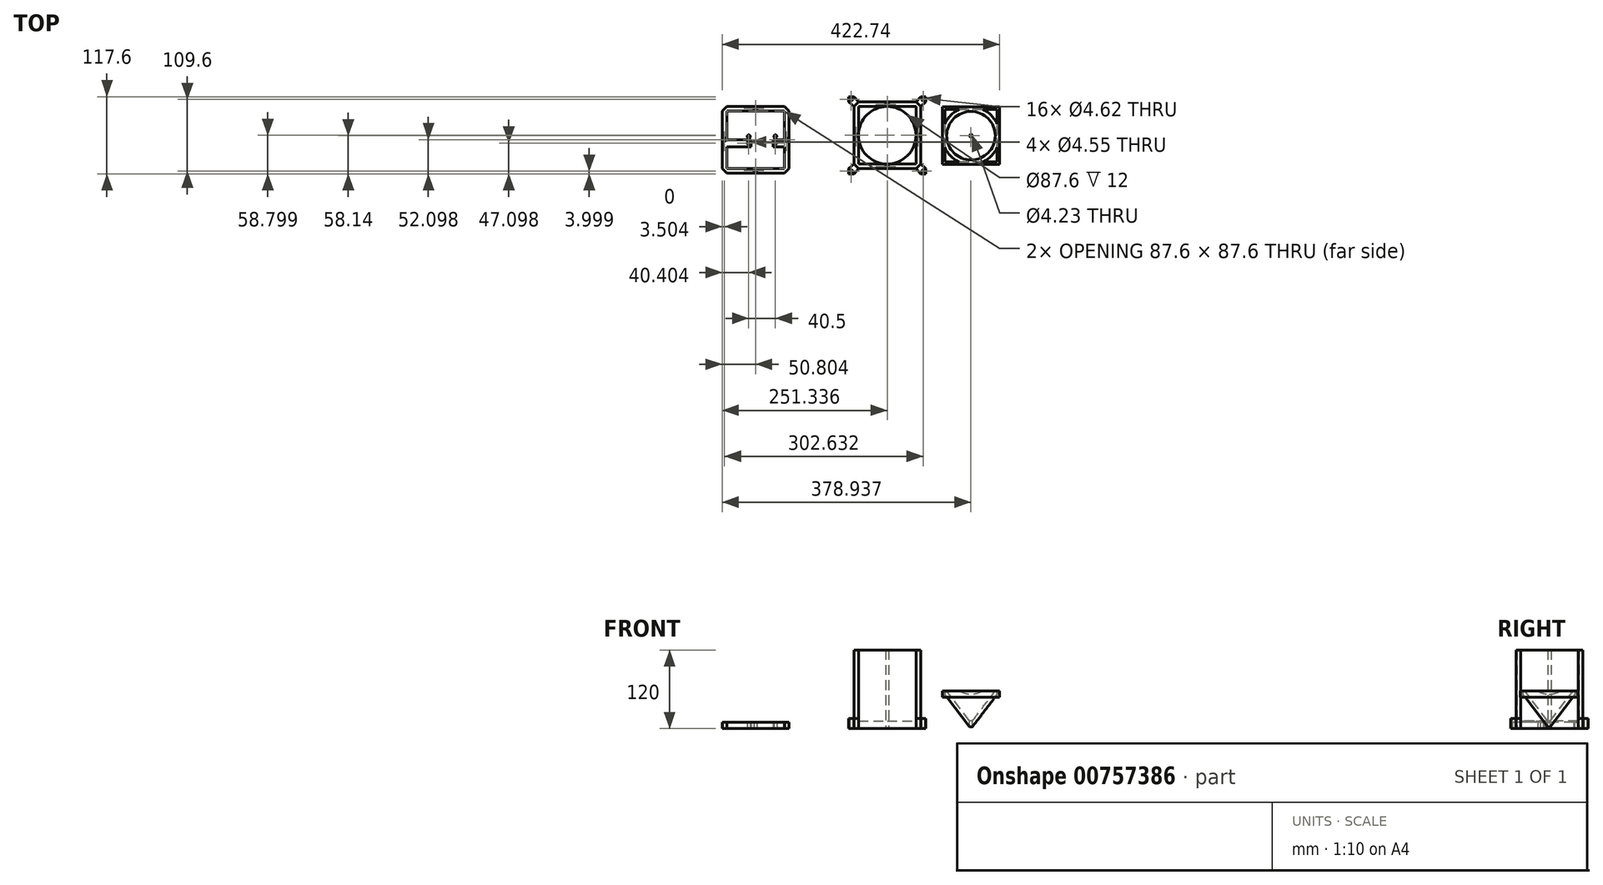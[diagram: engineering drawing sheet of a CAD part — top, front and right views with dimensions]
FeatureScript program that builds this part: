
annotation { "Feature Type Name" : "Feature", "Feature Type Description" : "" }
export const myFeature = defineFeature(function(context is Context, id is Id, definition is map)
    precondition{}
    {
        {
            var Q0;
            Q0=qCreatedBy(makeId("Top.planeOp"),FACE);
            var sketch = newSketch(context, id + "F0", { "sketchPlane" : qUnion([Q0])});
            skLineSegment(sketch, "E0.bottom", {"start": v(-49.4, 51.46) * mm, "end": v(38.2, 51.46) * mm});
            skLineSegment(sketch, "E0.top", {"start": v(-49.4, -50.14) * mm, "end": v(38.2, -50.14) * mm});
            skLineSegment(sketch, "E0.left", {"start": v(-56.4, 44.46) * mm, "end": v(-56.4, -43.14) * mm});
            skLineSegment(sketch, "E0.right", {"start": v(45.2, 44.46) * mm, "end": v(45.2, -43.14) * mm});
            skLineSegment(sketch, "E1.0", {"start": v(-49.4, 44.46) * mm, "end": v(38.2, 44.46) * mm});
            skLineSegment(sketch, "E1.1", {"start": v(-49.4, 44.46) * mm, "end": v(-49.4, -43.14) * mm});
            skLineSegment(sketch, "E1.2", {"start": v(-49.4, -43.14) * mm, "end": v(38.2, -43.14) * mm});
            skLineSegment(sketch, "E1.3", {"start": v(38.2, 44.46) * mm, "end": v(38.2, -43.14) * mm});
            skLineSegment(sketch, "E2.top", {"start": v(-56.4, 59.46) * mm, "end": v(-64.4, 59.46) * mm});
            skLineSegment(sketch, "E2.right", {"start": v(-64.4, 51.46) * mm, "end": v(-64.4, 59.46) * mm});
            skLineSegment(sketch, "E3.top", {"start": v(45.2, 59.46) * mm, "end": v(53.2, 59.46) * mm});
            skLineSegment(sketch, "E3.right", {"start": v(53.2, 51.46) * mm, "end": v(53.2, 59.46) * mm});
            skLineSegment(sketch, "E4.top", {"start": v(45.2, -58.14) * mm, "end": v(53.2, -58.14) * mm});
            skLineSegment(sketch, "E4.right", {"start": v(53.2, -50.14) * mm, "end": v(53.2, -58.14) * mm});
            skLineSegment(sketch, "E5.top", {"start": v(-56.4, -58.14) * mm, "end": v(-64.4, -58.14) * mm});
            skLineSegment(sketch, "E5.right", {"start": v(-64.4, -50.14) * mm, "end": v(-64.4, -58.14) * mm});
            skCircle(sketch, "E6", {"center": v(-60.4, 55.46) * mm, "radius": 2.31 * mm});
            skCircle(sketch, "E7", {"center": v(-60.4, -54.14) * mm, "radius": 2.31 * mm});
            skCircle(sketch, "E8", {"center": v(49.2, -54.14) * mm, "radius": 2.31 * mm});
            skCircle(sketch, "E9", {"center": v(49.2, 55.46) * mm, "radius": 2.31 * mm});
            skLineSegment(sketch, "E10", {"start": v(-64.4, 51.46) * mm, "end": v(-56.4, 44.46) * mm});
            skLineSegment(sketch, "E11", {"start": v(-56.4, 59.46) * mm, "end": v(-49.4, 51.46) * mm});
            skLineSegment(sketch, "E12", {"start": v(-64.4, -50.14) * mm, "end": v(-56.4, -43.14) * mm});
            skLineSegment(sketch, "E13", {"start": v(-56.4, -58.14) * mm, "end": v(-49.4, -50.14) * mm});
            skLineSegment(sketch, "E14", {"start": v(45.2, -58.14) * mm, "end": v(38.2, -50.14) * mm});
            skLineSegment(sketch, "E15", {"start": v(53.2, -50.14) * mm, "end": v(45.2, -43.14) * mm});
            skLineSegment(sketch, "E16", {"start": v(45.2, 59.46) * mm, "end": v(38.2, 51.46) * mm});
            skLineSegment(sketch, "E17", {"start": v(53.2, 51.46) * mm, "end": v(45.2, 44.46) * mm});
            skPoint(sketch, "E4.left.start.orphan", {"position": v(45.2, -50.14) * mm});
            skLineSegment(sketch, "E18", {"start": v(-56.4, 44.46) * mm, "end": v(-49.4, 51.46) * mm});
            skLineSegment(sketch, "E19", {"start": v(38.2, 51.46) * mm, "end": v(45.2, 44.46) * mm});
            skLineSegment(sketch, "E20", {"start": v(-56.4, -43.14) * mm, "end": v(-49.4, -50.14) * mm});
            skLineSegment(sketch, "E21", {"start": v(38.2, -50.14) * mm, "end": v(45.2, -43.14) * mm});
            skCircle(sketch, "E22", {"center": v(-5.6, 0.66) * mm, "radius": 43.8 * mm});
            skCircle(sketch, "E23", {"center": v(-5.6, 47.96) * mm, "radius": 2.31 * mm});
            skCircle(sketch, "E24", {"center": v(-52.9, 0.66) * mm, "radius": 2.31 * mm});
            skCircle(sketch, "E25", {"center": v(41.7, 0.66) * mm, "radius": 2.31 * mm});
            skCircle(sketch, "E26", {"center": v(-5.6, -46.64) * mm, "radius": 2.31 * mm});
            skLineSegment(sketch, "E27.bottom", {"start": v(-249.94, 44.76) * mm, "end": v(-162.34, 44.76) * mm});
            skLineSegment(sketch, "E27.top", {"start": v(-249.94, -56.84) * mm, "end": v(-162.34, -56.84) * mm});
            skLineSegment(sketch, "E27.left", {"start": v(-256.94, 37.76) * mm, "end": v(-256.94, -49.84) * mm});
            skLineSegment(sketch, "E27.right", {"start": v(-155.34, 37.76) * mm, "end": v(-155.34, -49.84) * mm});
            skLineSegment(sketch, "E28.0", {"start": v(-249.94, 37.76) * mm, "end": v(-162.34, 37.76) * mm});
            skLineSegment(sketch, "E28.1", {"start": v(-249.94, 37.76) * mm, "end": v(-249.94, -49.84) * mm});
            skLineSegment(sketch, "E28.2", {"start": v(-249.94, -49.84) * mm, "end": v(-162.34, -49.84) * mm});
            skLineSegment(sketch, "E28.3", {"start": v(-162.34, 37.76) * mm, "end": v(-162.34, -49.84) * mm});
            skLineSegment(sketch, "E29", {"start": v(-256.94, 37.76) * mm, "end": v(-249.94, 44.76) * mm});
            skLineSegment(sketch, "E30", {"start": v(-162.34, 44.76) * mm, "end": v(-155.34, 37.76) * mm});
            skLineSegment(sketch, "E31", {"start": v(-256.94, -49.84) * mm, "end": v(-249.94, -56.84) * mm});
            skLineSegment(sketch, "E32", {"start": v(-162.34, -56.84) * mm, "end": v(-155.34, -49.84) * mm});
            skCircle(sketch, "E33", {"center": v(-206.14, 41.26) * mm, "radius": 2.31 * mm});
            skCircle(sketch, "E34", {"center": v(-253.44, -6.04) * mm, "radius": 2.31 * mm});
            skCircle(sketch, "E35", {"center": v(-158.84, -6.04) * mm, "radius": 2.31 * mm});
            skCircle(sketch, "E36", {"center": v(-206.14, -53.34) * mm, "radius": 2.31 * mm});
            skPoint(sketch, "E37.middle", {"position": v(-206.14, -6.04) * mm});
            skPoint(sketch, "E37.middle.positionSnap0", {"position": v(-206.14, 37.76) * mm});
            skPoint(sketch, "E37.middle.positionSnap1", {"position": v(-249.94, -6.04) * mm});
            skPoint(sketch, "E37.centerSnap0", {"position": v(-206.14, 37.76) * mm});
            skPoint(sketch, "E37.centerSnap1", {"position": v(-249.94, -6.04) * mm});
            skCircle(sketch, "E38", {"center": v(-176.04, -11.04) * mm, "radius": 2.27 * mm});
            skCircle(sketch, "E39", {"center": v(-216.54, -11.04) * mm, "radius": 2.27 * mm});
            skLineSegment(sketch, "E40", {"start": v(-249.94, -6.04) * mm, "end": v(-162.34, -6.04) * mm});
            skCircle(sketch, "E41.MirrorC", {"center": v(-176.04, -1.04) * mm, "radius": 2.27 * mm});
            skCircle(sketch, "E42.MirrorC", {"center": v(-216.54, -1.04) * mm, "radius": 2.27 * mm});
            skLineSegment(sketch, "E43.bottom", {"start": v(-249.94, 6.48) * mm, "end": v(-213.04, 6.48) * mm});
            skLineSegment(sketch, "E43.top", {"start": v(-249.94, -16.78) * mm, "end": v(-213.04, -16.78) * mm});
            skLineSegment(sketch, "E43.left", {"start": v(-249.94, 6.48) * mm, "end": v(-249.94, -16.78) * mm});
            skLineSegment(sketch, "E43.right", {"start": v(-213.04, 6.48) * mm, "end": v(-213.04, -16.78) * mm});
            skLineSegment(sketch, "E44.bottom", {"start": v(-162.34, 6.48) * mm, "end": v(-179.54, 6.48) * mm});
            skLineSegment(sketch, "E44.top", {"start": v(-162.34, -16.78) * mm, "end": v(-179.54, -16.78) * mm});
            skLineSegment(sketch, "E44.left", {"start": v(-162.34, 6.48) * mm, "end": v(-162.34, -16.78) * mm});
            skLineSegment(sketch, "E44.right", {"start": v(-179.54, 6.48) * mm, "end": v(-179.54, -16.78) * mm});
            skSolve(sketch);
        }
        {
            var Q0;
            Q0=makeQuery(id+"F0.imprint","IMPRINT",FACE,{"disambiguationData":[TD([[makeQuery(id+"F0.imprint","IMPRINT",EDGE,{"derivedFrom":sQuery(id+"F0.wireOp",EDGE,"E0.bottom")}),-1.0]])]});
            extrude(context, id + "F1", {"entities" : qUnion([Q0]), "depth" : 120 * mm, "offsetDistance" : 25 * mm});
        }
        {
            var Q0;
            Q0=makeQuery(id+"F0.imprint","IMPRINT",FACE,{"disambiguationData":[TD([[makeQuery(id+"F0.imprint","IMPRINT",EDGE,{"derivedFrom":sQuery(id+"F0.wireOp",EDGE,"E5.top")}),-1.0]])]});
            var Q1;
            Q1=makeQuery(id+"F0.imprint","IMPRINT",FACE,{"disambiguationData":[TD([[makeQuery(id+"F0.imprint","IMPRINT",EDGE,{"derivedFrom":sQuery(id+"F0.wireOp",EDGE,"E4.top")}),1.0]])]});
            var Q2;
            Q2=makeQuery(id+"F0.imprint","IMPRINT",FACE,{"disambiguationData":[TD([[makeQuery(id+"F0.imprint","IMPRINT",EDGE,{"derivedFrom":sQuery(id+"F0.wireOp",EDGE,"E3.top")}),-1.0]])]});
            var Q3;
            Q3=makeQuery(id+"F0.imprint","IMPRINT",FACE,{"disambiguationData":[TD([[makeQuery(id+"F0.imprint","IMPRINT",EDGE,{"derivedFrom":sQuery(id+"F0.wireOp",EDGE,"E2.top")}),1.0]])]});
            extrude(context, id + "F2", {"entities" : qUnion([Q0, Q1, Q2, Q3]), "operationType" : NewBodyOperationType.ADD, "depth" : 15.5 * mm, "offsetDistance" : 25 * mm});
        }
        {
            var Q0;
            {var subQ0=sQuery(id+"F0.wireOp",EDGE,"E1.1");var subQ1=sQuery(id+"F0.wireOp",EDGE,"E1.0");var subQ2=makeQuery(id+"F0.imprint","INTERSECT",VERTEX,{"derivedFrom":[subQ1,subQ0]});Q0=makeQuery(id+"F0.imprint","IMPRINT",FACE,{"disambiguationData":[TD([[makeQuery(id+"F0.imprint","IMPRINT",EDGE,{"disambiguationData":[TD([[subQ2,-1.0]])],"derivedFrom":subQ1}),-1.0]])]});}
            var Q1;
            {var subQ0=sQuery(id+"F0.wireOp",EDGE,"E1.3");var subQ1=sQuery(id+"F0.wireOp",EDGE,"E1.0");var subQ2=makeQuery(id+"F0.imprint","INTERSECT",VERTEX,{"derivedFrom":[subQ1,subQ0]});Q1=makeQuery(id+"F0.imprint","IMPRINT",FACE,{"disambiguationData":[TD([[makeQuery(id+"F0.imprint","IMPRINT",EDGE,{"disambiguationData":[TD([[subQ2,1.0]])],"derivedFrom":subQ1}),-1.0]])]});}
            var Q2;
            {var subQ0=sQuery(id+"F0.wireOp",EDGE,"E1.3");var subQ1=sQuery(id+"F0.wireOp",EDGE,"E1.2");var subQ2=makeQuery(id+"F0.imprint","INTERSECT",VERTEX,{"derivedFrom":[subQ1,subQ0]});Q2=makeQuery(id+"F0.imprint","IMPRINT",FACE,{"disambiguationData":[TD([[makeQuery(id+"F0.imprint","IMPRINT",EDGE,{"disambiguationData":[TD([[subQ2,1.0]])],"derivedFrom":subQ1}),1.0]])]});}
            var Q3;
            {var subQ0=sQuery(id+"F0.wireOp",EDGE,"E1.2");var subQ1=sQuery(id+"F0.wireOp",EDGE,"E1.1");var subQ2=makeQuery(id+"F0.imprint","INTERSECT",VERTEX,{"derivedFrom":[subQ1,subQ0]});Q3=makeQuery(id+"F0.imprint","IMPRINT",FACE,{"disambiguationData":[TD([[makeQuery(id+"F0.imprint","IMPRINT",EDGE,{"disambiguationData":[TD([[subQ2,1.0]])],"derivedFrom":subQ1}),1.0]])]});}
            extrude(context, id + "F3", {"entities" : qUnion([Q0, Q1, Q2, Q3]), "operationType" : NewBodyOperationType.ADD, "depth" : 12 * mm, "offsetDistance" : 25 * mm});
        }
        {
            var Q0;
            Q0=qCreatedBy(makeId("Front.planeOp"),FACE);
            var sketch = newSketch(context, id + "F4", { "sketchPlane" : qUnion([Q0])});
            skLineSegment(sketch, "E45.bottom", {"start": v(78.2, 57.63) * mm, "end": v(85.04, 57.63) * mm});
            skLineSegment(sketch, "E45.right", {"start": v(122, 57.63) * mm, "end": v(122, 0) * mm});
            skLineSegment(sketch, "E46", {"start": v(78.2, 57.63) * mm, "end": v(119.88, 2.78) * mm});
            skLineSegment(sketch, "E47", {"start": v(85.04, 57.63) * mm, "end": v(119.88, 11.8) * mm});
            skLineSegment(sketch, "E48", {"start": v(119.88, 11.8) * mm, "end": v(119.88, 2.78) * mm});
            skSolve(sketch);
        }
        {
            var Q0;
            Q0=makeQuery(id+"F4.imprint","IMPRINT",FACE,{"disambiguationData":[TD([[makeQuery(id+"F4.imprint","IMPRINT",EDGE,{"derivedFrom":sQuery(id+"F4.wireOp",EDGE,"E45.bottom")}),-1.0]])]});
            var Q1;
            Q1=sQuery(id+"F4.wireOp",EDGE,"E45.right");
            revolve(context, id + "F5", {"surfaceOperationType" : NewSurfaceOperationType.NEW, "entities" : qUnion([Q0]), "axis" : qUnion([Q1]), "revolveType" : RevolveType.FULL});
        }
        {
            var Q0;
            Q0=makeQuery(id+"F5.opRevolve","SWEPT_FACE",FACE,{"disambiguationData":[OSD([sQuery(id+"F4.wireOp",EDGE,"E45.bottom")])]});
            var sketch = newSketch(context, id + "F6", { "sketchPlane" : qUnion([Q0])});
            skLineSegment(sketch, "E49.bottom", {"start": v(165.8, 43.8) * mm, "end": v(78.2, 43.8) * mm});
            skLineSegment(sketch, "E49.top", {"start": v(165.8, -43.8) * mm, "end": v(78.2, -43.8) * mm});
            skLineSegment(sketch, "E49.left", {"start": v(165.8, 43.8) * mm, "end": v(165.8, -43.8) * mm});
            skLineSegment(sketch, "E49.right", {"start": v(78.2, 43.8) * mm, "end": v(78.2, -43.8) * mm});
            skPoint(sketch, "E49.middle", {"position": v(122, 0) * mm});
            skLineSegment(sketch, "E50.bottom", {"start": v(162, 40) * mm, "end": v(82, 40) * mm});
            skLineSegment(sketch, "E50.top", {"start": v(162, -40) * mm, "end": v(82, -40) * mm});
            skLineSegment(sketch, "E50.left", {"start": v(162, 40) * mm, "end": v(162, -40) * mm});
            skLineSegment(sketch, "E50.right", {"start": v(82, 40) * mm, "end": v(82, -40) * mm});
            skSolve(sketch);
        }
        {
            var Q0;
            {var subQ6=sQuery(id+"F6.wireOp",EDGE,"E49.left");var subQ8=sQuery(id+"F6.wireOp",EDGE,"E49.bottom");var subQ9=makeQuery(id+"F6.imprint","INTERSECT",VERTEX,{"derivedFrom":[subQ8,subQ6]});Q0=makeQuery(id+"F6.imprint","IMPRINT",FACE,{"disambiguationData":[TD([[makeQuery(id+"F6.imprint","IMPRINT",EDGE,{"disambiguationData":[TD([[subQ9,-1.0]])],"derivedFrom":subQ8}),1.0]])]});}
            var Q1;
            {var subQ5=sQuery(id+"F6.wireOp",EDGE,"E49.right");var subQ6=sQuery(id+"F6.wireOp",EDGE,"E49.bottom");var subQ7=makeQuery(id+"F6.imprint","INTERSECT",VERTEX,{"derivedFrom":[subQ6,subQ5]});Q1=makeQuery(id+"F6.imprint","IMPRINT",FACE,{"disambiguationData":[TD([[makeQuery(id+"F6.imprint","IMPRINT",EDGE,{"disambiguationData":[TD([[subQ7,1.0]])],"derivedFrom":subQ6}),1.0]])]});}
            var Q2;
            {var subQ0=sQuery(id+"F6.wireOp",EDGE,"E50.right");var subQ1=makeQuery(id+"F5.opRevolve","SWEPT_EDGE",EDGE,{"disambiguationData":[OSD([sQuery(id+"F4.wireOp",EDGE,"E45.bottom"),sQuery(id+"F4.wireOp",EDGE,"E46")])]});var subQ2=makeQuery(id+"F6.imprint","INTERSECT",VERTEX,{"disambiguationData":[OD(0.0)],"derivedFrom":[subQ1,subQ0]});Q2=makeQuery(id+"F6.imprint","IMPRINT",FACE,{"disambiguationData":[TD([[makeQuery(id+"F6.imprint","IMPRINT",EDGE,{"disambiguationData":[TD([[subQ2,-1.0]])],"derivedFrom":subQ0}),-1.0]])]});}
            var Q3;
            {var subQ5=sQuery(id+"F6.wireOp",EDGE,"E49.right");var subQ6=sQuery(id+"F6.wireOp",EDGE,"E49.top");var subQ7=makeQuery(id+"F6.imprint","INTERSECT",VERTEX,{"derivedFrom":[subQ6,subQ5]});Q3=makeQuery(id+"F6.imprint","IMPRINT",FACE,{"disambiguationData":[TD([[makeQuery(id+"F6.imprint","IMPRINT",EDGE,{"disambiguationData":[TD([[subQ7,1.0]])],"derivedFrom":subQ6}),-1.0]])]});}
            var Q4;
            {var subQ5=sQuery(id+"F6.wireOp",EDGE,"E49.left");var subQ6=sQuery(id+"F6.wireOp",EDGE,"E49.top");var subQ7=makeQuery(id+"F6.imprint","INTERSECT",VERTEX,{"derivedFrom":[subQ6,subQ5]});Q4=makeQuery(id+"F6.imprint","IMPRINT",FACE,{"disambiguationData":[TD([[makeQuery(id+"F6.imprint","IMPRINT",EDGE,{"disambiguationData":[TD([[subQ7,-1.0]])],"derivedFrom":subQ6}),-1.0]])]});}
            var Q5;
            {var subQ0=sQuery(id+"F6.wireOp",EDGE,"E50.top");var subQ1=makeQuery(id+"F5.opRevolve","SWEPT_EDGE",EDGE,{"disambiguationData":[OSD([sQuery(id+"F4.wireOp",EDGE,"E45.bottom"),sQuery(id+"F4.wireOp",EDGE,"E46")])]});var subQ2=makeQuery(id+"F6.imprint","INTERSECT",VERTEX,{"disambiguationData":[OD(0.0)],"derivedFrom":[subQ1,subQ0]});Q5=makeQuery(id+"F6.imprint","IMPRINT",FACE,{"disambiguationData":[TD([[makeQuery(id+"F6.imprint","IMPRINT",EDGE,{"disambiguationData":[TD([[subQ2,-1.0]])],"derivedFrom":subQ0}),1.0]])]});}
            var Q6;
            {var subQ0=sQuery(id+"F6.wireOp",EDGE,"E50.bottom");var subQ1=makeQuery(id+"F5.opRevolve","SWEPT_EDGE",EDGE,{"disambiguationData":[OSD([sQuery(id+"F4.wireOp",EDGE,"E45.bottom"),sQuery(id+"F4.wireOp",EDGE,"E46")])]});var subQ2=makeQuery(id+"F6.imprint","INTERSECT",VERTEX,{"disambiguationData":[OD(0.0)],"derivedFrom":[subQ1,subQ0]});Q6=makeQuery(id+"F6.imprint","IMPRINT",FACE,{"disambiguationData":[TD([[makeQuery(id+"F6.imprint","IMPRINT",EDGE,{"disambiguationData":[TD([[subQ2,-1.0]])],"derivedFrom":subQ0}),-1.0]])]});}
            var Q7;
            {var subQ0=sQuery(id+"F6.wireOp",EDGE,"E50.left");var subQ1=makeQuery(id+"F5.opRevolve","SWEPT_EDGE",EDGE,{"disambiguationData":[OSD([sQuery(id+"F4.wireOp",EDGE,"E45.bottom"),sQuery(id+"F4.wireOp",EDGE,"E46")])]});var subQ2=makeQuery(id+"F6.imprint","INTERSECT",VERTEX,{"disambiguationData":[OD(0.0)],"derivedFrom":[subQ1,subQ0]});Q7=makeQuery(id+"F6.imprint","IMPRINT",FACE,{"disambiguationData":[TD([[makeQuery(id+"F6.imprint","IMPRINT",EDGE,{"disambiguationData":[TD([[subQ2,-1.0]])],"derivedFrom":subQ0}),1.0]])]});}
            extrude(context, id + "F7", {"entities" : qUnion([Q0, Q1, Q2, Q3, Q4, Q5, Q6, Q7]), "operationType" : NewBodyOperationType.ADD, "oppositeDirection" : true, "depth" : 10 * mm, "offsetDistance" : 25 * mm});
        }
        {
            var Q0;
            Q0=makeQuery(id+"F0.imprint","IMPRINT",FACE,{"disambiguationData":[TD([[makeQuery(id+"F0.imprint","IMPRINT",EDGE,{"derivedFrom":sQuery(id+"F0.wireOp",EDGE,"E27.bottom")}),-1.0]])]});
            var Q1;
            Q1=makeQuery(id+"F0.imprint","IMPRINT",FACE,{"disambiguationData":[TD([[makeQuery(id+"F0.imprint","IMPRINT",EDGE,{"derivedFrom":sQuery(id+"F0.wireOp",EDGE,"E42.MirrorC")}),1.0]])]});
            var Q2;
            Q2=makeQuery(id+"F0.imprint","IMPRINT",FACE,{"disambiguationData":[TD([[makeQuery(id+"F0.imprint","IMPRINT",EDGE,{"derivedFrom":sQuery(id+"F0.wireOp",EDGE,"E39")}),-1.0]])]});
            var Q3;
            Q3=makeQuery(id+"F0.imprint","IMPRINT",FACE,{"disambiguationData":[TD([[makeQuery(id+"F0.imprint","IMPRINT",EDGE,{"derivedFrom":sQuery(id+"F0.wireOp",EDGE,"E41.MirrorC")}),1.0]])]});
            var Q4;
            Q4=makeQuery(id+"F0.imprint","IMPRINT",FACE,{"disambiguationData":[TD([[makeQuery(id+"F0.imprint","IMPRINT",EDGE,{"derivedFrom":sQuery(id+"F0.wireOp",EDGE,"E38")}),-1.0]])]});
            extrude(context, id + "F8", {"entities" : qUnion([Q0, Q1, Q2, Q3, Q4]), "depth" : 10 * mm, "offsetDistance" : 25 * mm});
        }
    });
